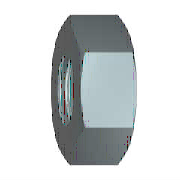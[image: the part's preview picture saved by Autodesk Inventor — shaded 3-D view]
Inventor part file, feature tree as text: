
AUTODESK INVENTOR PART (.ipt)
format: ipt  version: 2013 (Build 170138000, 138)  size: 173,056 bytes
history: native  units: mm (DEFAULTED — no unit token found)
features: sketch x3, chamfer x1, hole x1, other x1, plane x1
ambient origin geometry x7: Origin, YZ Plane, XZ Plane, X Axis, Y Axis, Z Axis, Center Point
bodies: Solid1 (feature_tree), Body (feature_tree)
feature tree (7):
  chamfer  "Chamfer1"  Distance=4.363323mm
  hole  "Thread"  [1 undecoded]
  other  "Work Axis1"
  plane  "Work Plane1"
  sketch  "Sketch1"  dims[d0=8.082904mm]
  sketch  "Sketch2"  dims[d1=3.2mm]
  sketch  "Sketch3"  dims[d2=0.0mm d3=4.363323mm d4=4.363323mm d5=7.0mm d6=7.0mm d7=90.0deg d25=3.242mm d26=6.0mm d27=4.0mm d28=2.0mm d29=14.3117mm d30=8.0mm d31=20.594885mm d8=0.378886mm d9=30.0deg d10=0.378886mm d11=30.0deg d13=0.0mm d14=0.0mm d39=0.0mm d40=0.378886mm d41=0.378886mm d42=0.0mm]
note: 1 required parameter value undecoded (feature->parameter linkage not recoverable at this tier; creation-order binding heuristic only, values carry confidence <= 0.55)
